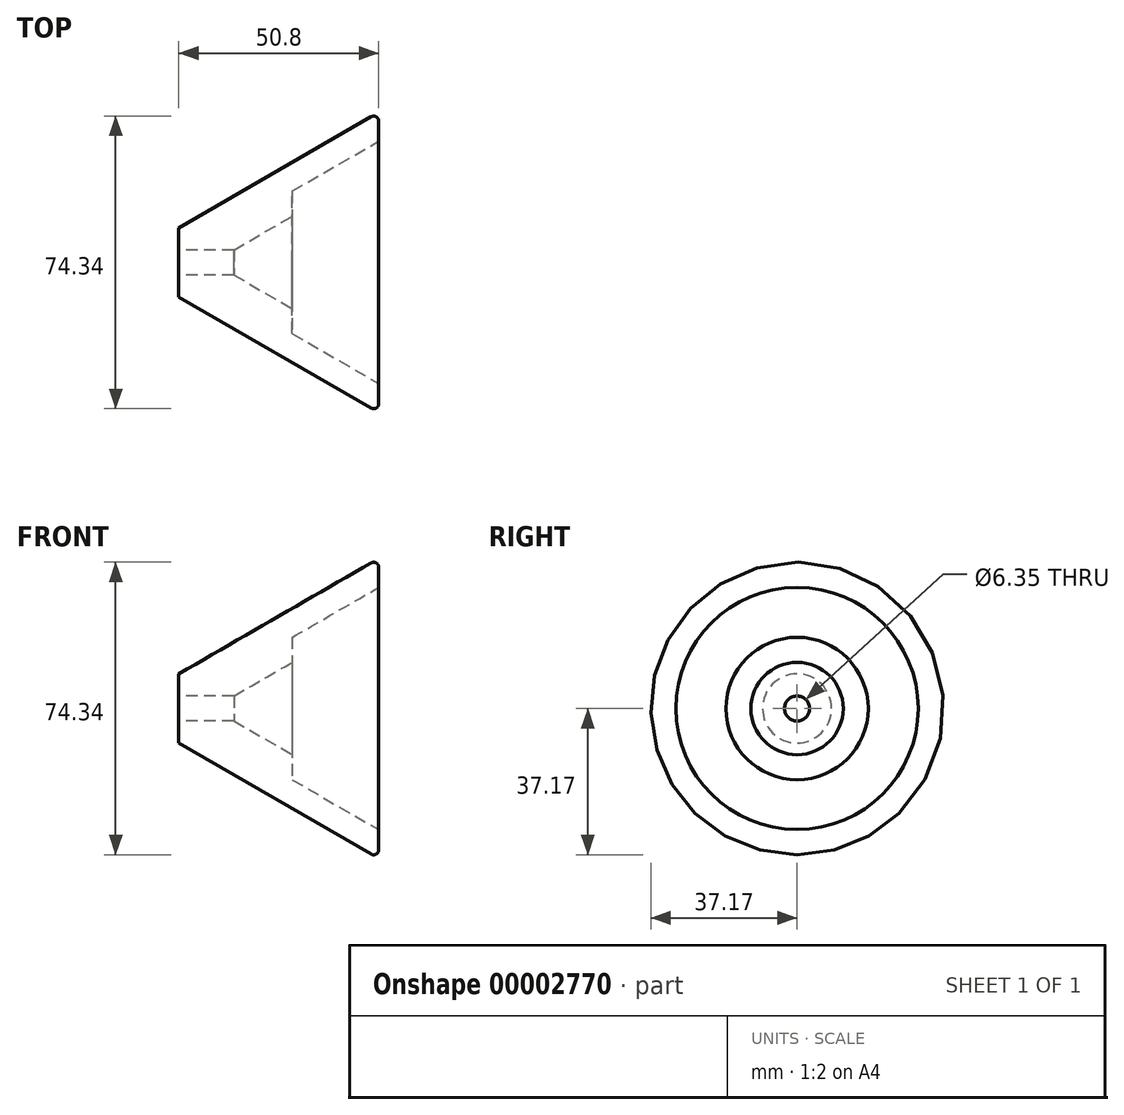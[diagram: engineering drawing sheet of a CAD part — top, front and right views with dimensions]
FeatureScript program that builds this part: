
annotation { "Feature Type Name" : "Feature", "Feature Type Description" : "" }
export const myFeature = defineFeature(function(context is Context, id is Id, definition is map)
    precondition{}
    {
        {
            var Q0;
            Q0=qCreatedBy(makeId("Front.planeOp"),FACE);
            var sketch = newSketch(context, id + "F0", { "sketchPlane" : qUnion([Q0])});
            skLineSegment(sketch, "E0", {"start": v(0, 0) * mm, "end": v(49.6, 0) * mm, "construction": true});
            skLineSegment(sketch, "E1", {"start": v(24.2, 0) * mm, "end": v(24.2, 8.93) * mm, "construction": true});
            skLineSegment(sketch, "E2", {"start": v(24.2, 17.07) * mm, "end": v(49.6, 17.07) * mm, "construction": true});
            skLineSegment(sketch, "E3", {"start": v(49.6, 17.07) * mm, "end": v(49.6, 0) * mm, "construction": true});
            skLineSegment(sketch, "E4", {"start": v(15.47, 8.93) * mm, "end": v(0, 0) * mm, "construction": true});
            skLineSegment(sketch, "E5", {"start": v(15.47, 8.93) * mm, "end": v(24.2, 8.93) * mm, "construction": true});
            skLineSegment(sketch, "E6", {"start": v(24.2, 8.93) * mm, "end": v(24.2, 17.07) * mm, "construction": true});
            skLineSegment(sketch, "E7.rect.left", {"start": v(42.3, 38.1) * mm, "end": v(42.3, 0) * mm});
            skLineSegment(sketch, "E7.rect.right", {"start": v(-8.5, 8.77) * mm, "end": v(-8.5, 0) * mm});
            skPoint(sketch, "E7.rect.middle", {"position": v(16.9, 0) * mm});
            skLineSegment(sketch, "E8", {"start": v(-8.5, 8.77) * mm, "end": v(42.3, 38.1) * mm});
            skLineSegment(sketch, "E9", {"start": v(42.3, 0) * mm, "end": v(-8.5, 0) * mm});
            skLineSegment(sketch, "E10", {"start": v(0, 0) * mm, "end": v(20.32, 11.73) * mm});
            skLineSegment(sketch, "E11", {"start": v(20.32, 11.73) * mm, "end": v(20.32, 18.08) * mm});
            skLineSegment(sketch, "E12", {"start": v(20.32, 18.08) * mm, "end": v(42.3, 30.77) * mm});
            skLineSegment(sketch, "E13", {"start": v(-8.5, 3.17) * mm, "end": v(5.5, 3.17) * mm});
            skSolve(sketch);
        }
        {
            var Q0;
            {var subQ4=sQuery(id+"F0.wireOp",EDGE,"E8");Q0=makeQuery(id+"F0.imprint","IMPRINT",FACE,{"disambiguationData":[TD([[makeQuery(id+"F0.imprint","IMPRINT",EDGE,{"derivedFrom":subQ4}),-1.0]])]});}
            var Q1;
            Q1=sQuery(id+"F0.wireOp",EDGE,"E0");
            revolve(context, id + "F1", {"entities" : qUnion([Q0]), "axis" : qUnion([Q1]), "revolveType" : RevolveType.FULL});
        }
        {
            var Q0;
            Q0=makeQuery(id+"F1.opRevolve","SWEPT_EDGE",EDGE,{"disambiguationData":[OSD([sQuery(id+"F0.wireOp",EDGE,"E7.rect.left"),sQuery(id+"F0.wireOp",EDGE,"E8")])]});
            fillet(context, id + "F2", {"entities" : qUnion([Q0]), "radius" : 1.27 * mm, "tangentPropagation" : true, "allowEdgeOverflow" : false});
        }
    });
